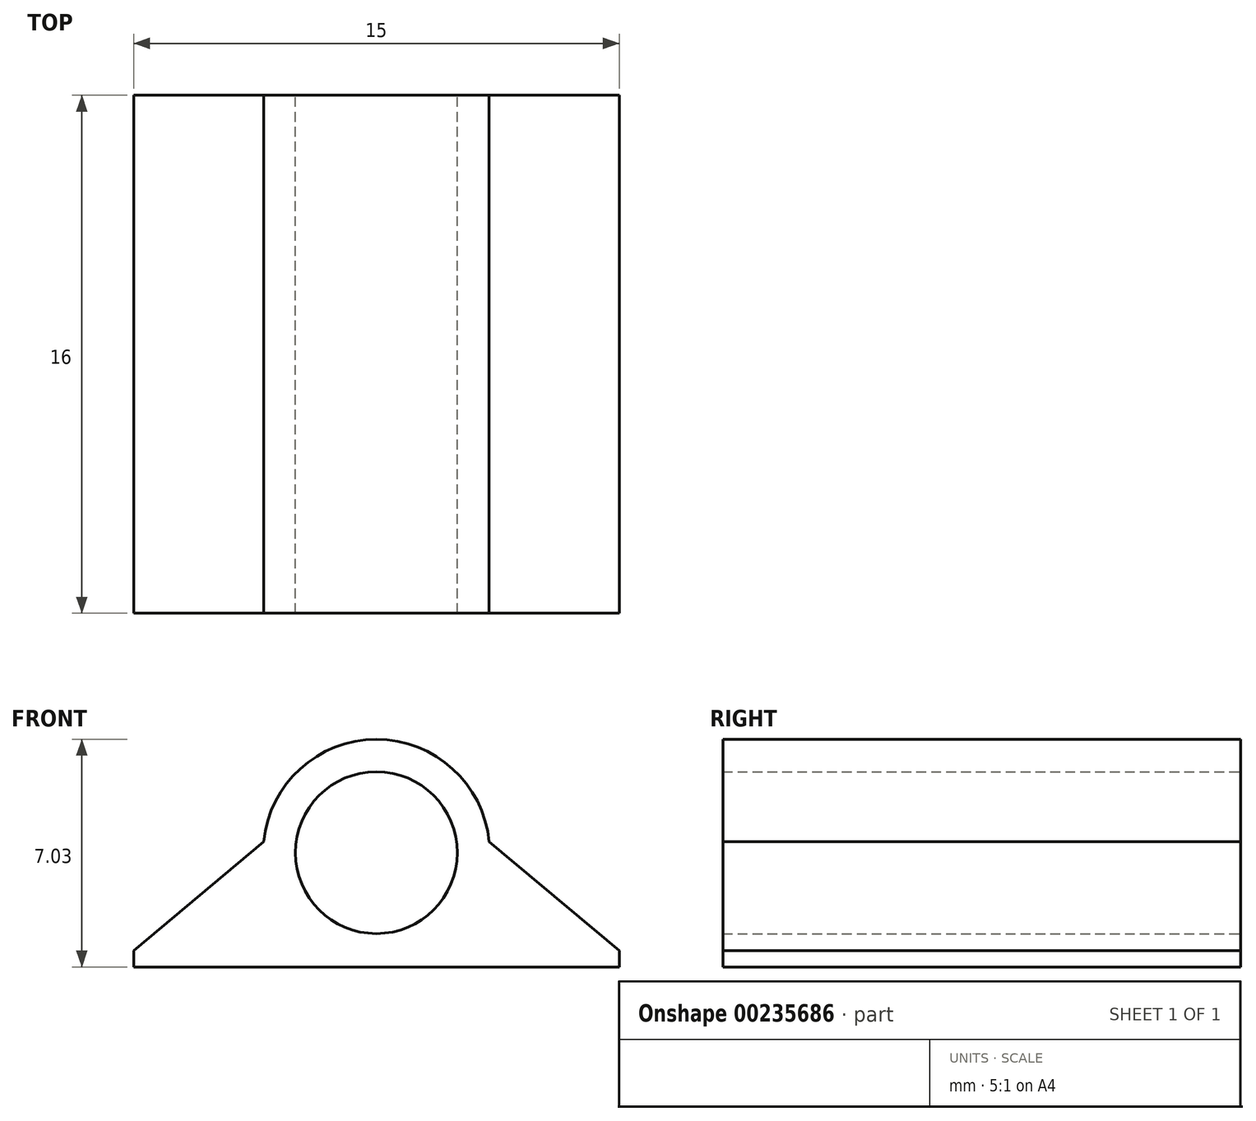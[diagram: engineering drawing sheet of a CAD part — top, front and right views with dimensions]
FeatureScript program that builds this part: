
annotation { "Feature Type Name" : "Feature", "Feature Type Description" : "" }
export const myFeature = defineFeature(function(context is Context, id is Id, definition is map)
    precondition{}
    {
        {
            var Q0;
            Q0=qCreatedBy(makeId("Front.planeOp"),FACE);
            var sketch = newSketch(context, id + "F0", { "sketchPlane" : qUnion([Q0])});
            skLineSegment(sketch, "E0", {"start": v(0, 0) * mm, "end": v(-15, 0) * mm});
            skLineSegment(sketch, "E1", {"start": v(-15, 0) * mm, "end": v(-15, 0.5) * mm});
            skLineSegment(sketch, "E2", {"start": v(0, 0.5) * mm, "end": v(0, 0) * mm});
            skCircle(sketch, "E3", {"center": v(-7.5, 3.53) * mm, "radius": 2.5 * mm});
            skArc(sketch, "E4", {"start": v(-4.02, 3.87) * mm, "mid": v(-7.5, 7.03) * mm, "end": v(-10.98, 3.87) * mm});
            skLineSegment(sketch, "E5", {"start": v(-15, 0.5) * mm, "end": v(-10.98, 3.87) * mm});
            skLineSegment(sketch, "E6", {"start": v(0, 0.5) * mm, "end": v(-4.02, 3.87) * mm});
            skLineSegment(sketch, "E7", {"start": v(-15, 0.5) * mm, "end": v(0, 0.5) * mm, "construction": true});
            skSolve(sketch);
        }
        {
            var Q0;
            Q0 = qSketchRegion(id + "F0", true);
            extrude(context, id + "F1", {"entities" : qUnion([Q0]), "depth" : 16 * mm});
        }
    });
